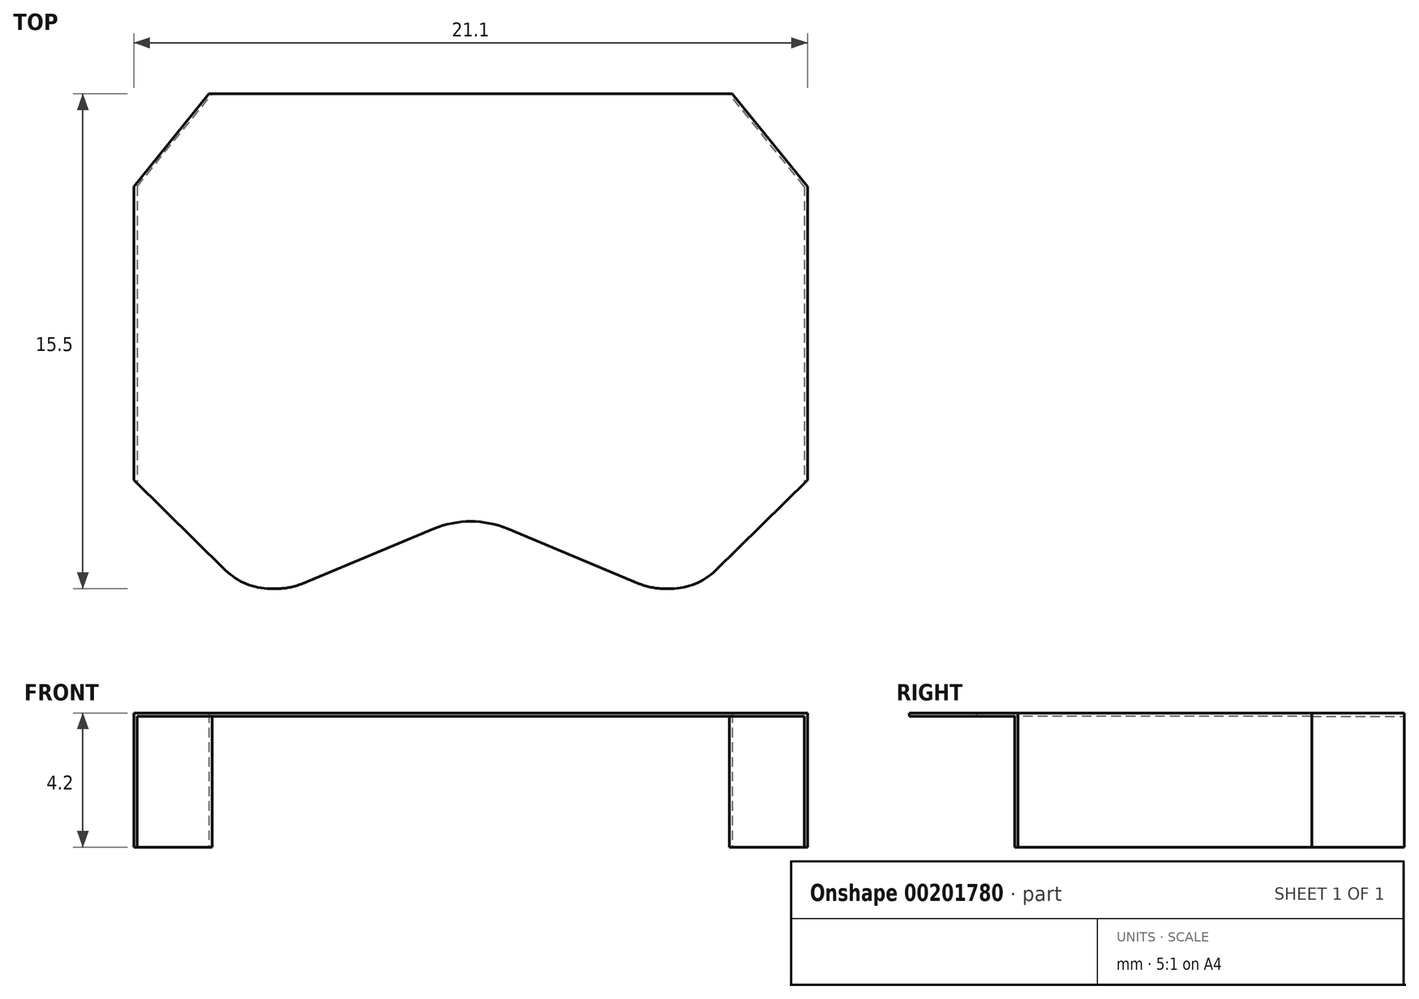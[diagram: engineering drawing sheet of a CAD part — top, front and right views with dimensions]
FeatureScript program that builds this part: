
annotation { "Feature Type Name" : "Feature", "Feature Type Description" : "" }
export const myFeature = defineFeature(function(context is Context, id is Id, definition is map)
    precondition{}
    {
        {
            var Q0;
            Q0=qCreatedBy(makeId("Top.planeOp"),FACE);
            var sketch = newSketch(context, id + "F0", { "sketchPlane" : qUnion([Q0])});
            skLineSegment(sketch, "E0", {"start": v(-8.2, 7.95) * mm, "end": v(-10.55, 5.05) * mm});
            skLineSegment(sketch, "E1", {"start": v(-10.55, -4.15) * mm, "end": v(-7.68, -6.98) * mm});
            skLineSegment(sketch, "E2", {"start": v(-10.55, 5.05) * mm, "end": v(-10.55, -4.15) * mm});
            skLineSegment(sketch, "E3", {"start": v(-8.2, 7.95) * mm, "end": v(0, 7.95) * mm});
            skLineSegment(sketch, "E4", {"start": v(-6.28, -7.55) * mm, "end": v(-6.05, -7.55) * mm});
            skLineSegment(sketch, "E5", {"start": v(-5.28, -7.4) * mm, "end": v(-1.16, -5.68) * mm});
            skLineSegment(sketch, "E6.MirrorCS", {"start": v(6.28, -7.55) * mm, "end": v(6.05, -7.55) * mm});
            skLineSegment(sketch, "E7.MirrorCS", {"start": v(8.2, 7.95) * mm, "end": v(0, 7.95) * mm});
            skLineSegment(sketch, "E8.MirrorCS", {"start": v(5.28, -7.4) * mm, "end": v(1.16, -5.68) * mm});
            skLineSegment(sketch, "E9.MirrorCS", {"start": v(10.55, -4.15) * mm, "end": v(7.68, -6.98) * mm});
            skLineSegment(sketch, "E10.MirrorCS", {"start": v(10.55, 5.05) * mm, "end": v(10.55, -4.15) * mm});
            skLineSegment(sketch, "E11.MirrorCS", {"start": v(8.2, 7.95) * mm, "end": v(10.55, 5.05) * mm});
            skPoint(sketch, "E12.visualSharp", {"position": v(0, -5.2) * mm});
            skArc(sketch, "E12.filletArc", {"start": v(1.16, -5.68) * mm, "mid": v(0, -5.44) * mm, "end": v(-1.16, -5.68) * mm});
            skPoint(sketch, "E13.visualSharp", {"position": v(-7.1, -7.55) * mm});
            skArc(sketch, "E13.filletArc", {"start": v(-7.68, -6.98) * mm, "mid": v(-7.03, -7.4) * mm, "end": v(-6.28, -7.55) * mm});
            skPoint(sketch, "E14.visualSharp", {"position": v(-5.65, -7.55) * mm});
            skArc(sketch, "E14.filletArc", {"start": v(-6.05, -7.55) * mm, "mid": v(-5.65, -7.51) * mm, "end": v(-5.28, -7.4) * mm});
            skPoint(sketch, "E15.visualSharp", {"position": v(5.65, -7.55) * mm});
            skArc(sketch, "E15.filletArc", {"start": v(5.28, -7.4) * mm, "mid": v(5.65, -7.51) * mm, "end": v(6.05, -7.55) * mm});
            skPoint(sketch, "E16.visualSharp", {"position": v(7.1, -7.55) * mm});
            skArc(sketch, "E16.filletArc", {"start": v(6.28, -7.55) * mm, "mid": v(7.03, -7.4) * mm, "end": v(7.68, -6.98) * mm});
            skSolve(sketch);
        }
        {
            var Q0;
            Q0=qSketchRegion(id+"F0",true);
            extrude(context, id + "F1", {"entities" : qUnion([Q0]), "depth" : 4.2 * mm});
        }
        {
            var Q0;
            Q0=makeQuery(id+"F1.opExtrude","SWEPT_FACE",FACE,{"disambiguationData":[OSD([sQuery(id+"F0.wireOp",EDGE,"E4")])]});
            var sketch = newSketch(context, id + "F2", { "sketchPlane" : qUnion([Q0])});
            skLineSegment(sketch, "E17.bottom", {"start": v(-10.45, 0) * mm, "end": v(10.45, 0) * mm});
            skLineSegment(sketch, "E17.top", {"start": v(-10.45, 4.1) * mm, "end": v(10.45, 4.1) * mm});
            skLineSegment(sketch, "E17.left", {"start": v(-10.45, 0) * mm, "end": v(-10.45, 4.1) * mm});
            skLineSegment(sketch, "E17.right", {"start": v(10.45, 0) * mm, "end": v(10.45, 4.1) * mm});
            skSolve(sketch);
        }
        {
            var Q0;
            Q0=qSketchRegion(id+"F2",true);
            extrude(context, id + "F3", {"entities" : qUnion([Q0]), "operationType" : NewBodyOperationType.REMOVE, "oppositeDirection" : true, "depth" : 10 * mm});
        }
        {
            var Q0;
            Q0=makeQuery(id+"F1.opExtrude","CAP_FACE",FACE,{"disambiguationData":[OSD([sQuery(id+"F0.wireOp",EDGE,"E0"),sQuery(id+"F0.wireOp",EDGE,"E1"),sQuery(id+"F0.wireOp",EDGE,"E2"),sQuery(id+"F0.wireOp",EDGE,"E3"),sQuery(id+"F0.wireOp",EDGE,"E4"),sQuery(id+"F0.wireOp",EDGE,"E5"),sQuery(id+"F0.wireOp",EDGE,"E6.MirrorCS"),sQuery(id+"F0.wireOp",EDGE,"E7.MirrorCS"),sQuery(id+"F0.wireOp",EDGE,"E8.MirrorCS"),sQuery(id+"F0.wireOp",EDGE,"E9.MirrorCS"),sQuery(id+"F0.wireOp",EDGE,"E10.MirrorCS"),sQuery(id+"F0.wireOp",EDGE,"E11.MirrorCS"),sQuery(id+"F0.wireOp",EDGE,"E12.filletArc"),sQuery(id+"F0.wireOp",EDGE,"E13.filletArc"),sQuery(id+"F0.wireOp",EDGE,"E14.filletArc"),sQuery(id+"F0.wireOp",EDGE,"E15.filletArc"),sQuery(id+"F0.wireOp",EDGE,"E16.filletArc")])],"isStart":true});
            var sketch = newSketch(context, id + "F4", { "sketchPlane" : qUnion([Q0])});
            skLineSegment(sketch, "E18", {"start": v(-10.45, -2.45) * mm, "end": v(-10.45, -5.05) * mm});
            skLineSegment(sketch, "E19", {"start": v(-10.45, -5.05) * mm, "end": v(-7.22, -9.04) * mm});
            skLineSegment(sketch, "E20", {"start": v(10.45, -2.45) * mm, "end": v(10.45, -5.05) * mm});
            skLineSegment(sketch, "E21", {"start": v(10.45, -5.05) * mm, "end": v(7.21, -9.05) * mm});
            skLineSegment(sketch, "E22", {"start": v(7.21, -9.05) * mm, "end": v(-7.22, -9.04) * mm});
            skLineSegment(sketch, "E23", {"start": v(-10.45, -2.45) * mm, "end": v(10.45, -2.45) * mm});
            skSolve(sketch);
        }
        {
            var Q0;
            Q0=qSketchRegion(id+"F4",true);
            extrude(context, id + "F5", {"entities" : qUnion([Q0]), "operationType" : NewBodyOperationType.REMOVE, "oppositeDirection" : true, "depth" : 4.1 * mm});
        }
    });
